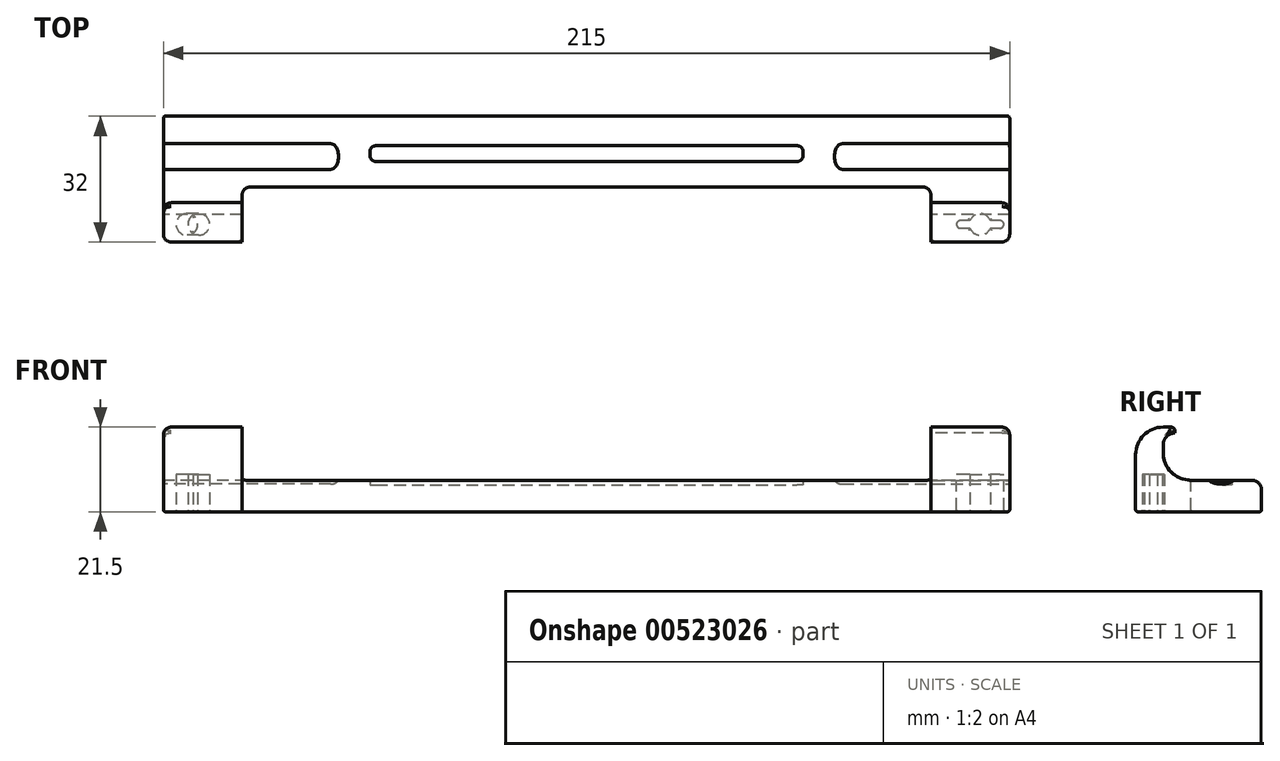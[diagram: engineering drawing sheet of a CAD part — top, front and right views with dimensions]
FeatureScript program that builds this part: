
annotation { "Feature Type Name" : "Feature", "Feature Type Description" : "" }
export const myFeature = defineFeature(function(context is Context, id is Id, definition is map)
    precondition{}
    {
        {
            var Q0;
            Q0=qCreatedBy(makeId("Right.planeOp"),FACE);
            var sketch = newSketch(context, id + "F0", { "sketchPlane" : qUnion([Q0])});
            skLineSegment(sketch, "E0", {"start": v(0, 0) * mm, "end": v(32, 0) * mm});
            skLineSegment(sketch, "E1", {"start": v(32, 0) * mm, "end": v(32, 8) * mm});
            skLineSegment(sketch, "E2", {"start": v(32, 8) * mm, "end": v(7, 8) * mm});
            skLineSegment(sketch, "E3", {"start": v(7, 8) * mm, "end": v(7, 21.5) * mm});
            skLineSegment(sketch, "E4", {"start": v(7, 21.5) * mm, "end": v(0, 21.5) * mm});
            skLineSegment(sketch, "E5", {"start": v(0, 21.5) * mm, "end": v(0, 0) * mm});
            skLineSegment(sketch, "E6", {"start": v(27.76, 8) * mm, "end": v(32, 3) * mm});
            skPoint(sketch, "E7", {"position": v(27.76, 8) * mm});
            skLineSegment(sketch, "E8.bottom", {"start": v(7, 21.5) * mm, "end": v(10, 21.5) * mm});
            skLineSegment(sketch, "E8.top", {"start": v(7, 17) * mm, "end": v(10, 17) * mm});
            skLineSegment(sketch, "E8.left", {"start": v(7, 21.5) * mm, "end": v(7, 17) * mm});
            skLineSegment(sketch, "E8.right", {"start": v(10, 21.5) * mm, "end": v(10, 17) * mm});
            skCircle(sketch, "E9", {"center": v(10, 17) * mm, "radius": 3 * mm});
            skPoint(sketch, "E10", {"position": v(10, 20) * mm});
            skSolve(sketch);
        }
        {
            var Q0;
            Q0=qCreatedBy(makeId("Right.planeOp"),FACE);
            var sketch = newSketch(context, id + "F1", { "sketchPlane" : qUnion([Q0])});
            skLineSegment(sketch, "E11.bottom", {"start": v(20.5, 8) * mm, "end": v(24.5, 8) * mm});
            skLineSegment(sketch, "E11.top", {"start": v(20.5, 6.8) * mm, "end": v(24.5, 6.8) * mm});
            skLineSegment(sketch, "E11.left", {"start": v(20.5, 8) * mm, "end": v(20.5, 6.8) * mm});
            skLineSegment(sketch, "E11.right", {"start": v(24.5, 8) * mm, "end": v(24.5, 6.8) * mm});
            skSolve(sketch);
        }
        {
            var Q0;
            {var subQ4=sQuery(id+"F0.wireOp",EDGE,"E0");Q0=makeQuery(id+"F0.imprint","IMPRINT",FACE,{"disambiguationData":[TD([[makeQuery(id+"F0.imprint","IMPRINT",EDGE,{"derivedFrom":subQ4}),1.0]])]});}
            var Q1;
            {var subQ0=sQuery(id+"F0.wireOp",EDGE,"E8.bottom");Q1=makeQuery(id+"F0.imprint","IMPRINT",FACE,{"disambiguationData":[TD([[makeQuery(id+"F0.imprint","IMPRINT",EDGE,{"derivedFrom":subQ0}),-1.0]])]});}
            var Q2;
            {var subQ3=sQuery(id+"F0.wireOp",EDGE,"E6");Q2=makeQuery(id+"F0.imprint","IMPRINT",FACE,{"disambiguationData":[TD([[makeQuery(id+"F0.imprint","IMPRINT",EDGE,{"derivedFrom":subQ3}),1.0]])]});}
            extrude(context, id + "F2", {"entities" : qUnion([Q0, Q1, Q2]), "endBound" : BoundingType.SYMMETRIC, "depth" : 215 * mm, "offsetDistance" : 25 * mm});
        }
        {
            var Q0;
            Q0 = qSketchRegion(id + "F1", true);
            extrude(context, id + "F3", {"entities" : qUnion([Q0]), "operationType" : NewBodyOperationType.REMOVE, "endBound" : BoundingType.SYMMETRIC, "oppositeDirection" : true, "depth" : 110 * mm, "offsetDistance" : 25 * mm});
        }
        {
            var Q0;
            Q0=makeQuery(id+"F2.opExtrude","SWEPT_FACE",FACE,{"disambiguationData":[OSD([sQuery(id+"F0.wireOp",EDGE,"E5")])]});
            var sketch = newSketch(context, id + "F4", { "sketchPlane" : qUnion([Q0])});
            skLineSegment(sketch, "E12", {"start": v(0, 50.18) * mm, "end": v(0, -36.06) * mm, "construction": true});
            skLineSegment(sketch, "E13.bottom", {"start": v(-87.5, 21.5) * mm, "end": v(87.5, 21.5) * mm});
            skLineSegment(sketch, "E13.top", {"start": v(-87.5, 8) * mm, "end": v(87.5, 8) * mm});
            skLineSegment(sketch, "E13.left", {"start": v(87.5, 21.5) * mm, "end": v(87.5, 8) * mm});
            skLineSegment(sketch, "E13.right", {"start": v(-87.5, 21.5) * mm, "end": v(-87.5, 8) * mm});
            skSolve(sketch);
        }
        {
            var Q0;
            Q0 = qSketchRegion(id + "F4", true);
            extrude(context, id + "F5", {"entities" : qUnion([Q0]), "operationType" : NewBodyOperationType.REMOVE, "endBound" : BoundingType.THROUGH_ALL, "oppositeDirection" : true, "depth" : 25 * mm, "offsetDistance" : 25 * mm});
        }
        {
            var Q0;
            Q0=makeQuery(id+"F5.boolean.opBoolean","MERGE",FACE,{"derivedFrom":[makeQuery(id+"F2.opExtrude","SWEPT_FACE",FACE,{"disambiguationData":[OSD([sQuery(id+"F0.wireOp",EDGE,"E2")])]}),makeQuery(id+"F5.opExtrude","SWEPT_FACE",FACE,{"disambiguationData":[OSD([sQuery(id+"F4.wireOp",EDGE,"E13.top")])]})]});
            var sketch = newSketch(context, id + "F6", { "sketchPlane" : qUnion([Q0])});
            skLineSegment(sketch, "E14.bottom", {"start": v(-87.5, 0) * mm, "end": v(87.5, 0) * mm});
            skLineSegment(sketch, "E14.top", {"start": v(-87.5, 14) * mm, "end": v(87.5, 14) * mm});
            skLineSegment(sketch, "E14.left", {"start": v(-87.5, 0) * mm, "end": v(-87.5, 14) * mm});
            skLineSegment(sketch, "E14.right", {"start": v(87.5, 0) * mm, "end": v(87.5, 14) * mm});
            skSolve(sketch);
        }
        {
            var Q0;
            Q0 = qSketchRegion(id + "F6", true);
            extrude(context, id + "F7", {"entities" : qUnion([Q0]), "operationType" : NewBodyOperationType.REMOVE, "endBound" : BoundingType.THROUGH_ALL, "oppositeDirection" : true, "depth" : 25 * mm, "offsetDistance" : 25 * mm});
        }
        {
            var Q0;
            Q0=makeQuery(id+"F2.opExtrude","CAP_FACE",FACE,{"disambiguationData":[OSD([sQuery(id+"F0.wireOp",EDGE,"E0"),sQuery(id+"F0.wireOp",EDGE,"E1"),sQuery(id+"F0.wireOp",EDGE,"E2"),sQuery(id+"F0.wireOp",EDGE,"E3"),sQuery(id+"F0.wireOp",EDGE,"E4"),sQuery(id+"F0.wireOp",EDGE,"E5"),sQuery(id+"F0.wireOp",EDGE,"E8.bottom"),sQuery(id+"F0.wireOp",EDGE,"E8.right"),sQuery(id+"F0.wireOp",EDGE,"E9")])],"isStart":true});
            var sketch = newSketch(context, id + "F8", { "sketchPlane" : qUnion([Q0])});
            skCircle(sketch, "E15", {"center": v(-21.75, 12.78) * mm, "radius": 5.78 * mm});
            skPoint(sketch, "E16", {"position": v(-25, 8) * mm});
            skPoint(sketch, "E17", {"position": v(-18.5, 8) * mm});
            skPoint(sketch, "E18", {"position": v(-21.75, 7) * mm});
            skSolve(sketch);
        }
        {
            var Q0;
            {var subQ0=sQuery(id+"F8.wireOp",EDGE,"E15");var subQ1=makeQuery(id+"F2.opExtrude","CAP_EDGE",EDGE,{"disambiguationData":[OSD([sQuery(id+"F0.wireOp",EDGE,"E2")])],"isStart":true});var subQ2=makeQuery(id+"F8.imprint","INTERSECT",VERTEX,{"disambiguationData":[OD(0.0)],"derivedFrom":[subQ1,subQ0]});Q0=makeQuery(id+"F8.imprint","IMPRINT",FACE,{"disambiguationData":[TD([[makeQuery(id+"F8.imprint","IMPRINT",EDGE,{"disambiguationData":[TD([[subQ2,-1.0]])],"derivedFrom":subQ0}),1.0]])]});}
            var Q1;
            {var subQ0=sQuery(id+"F8.wireOp",EDGE,"E15");var subQ1=makeQuery(id+"F2.opExtrude","CAP_EDGE",EDGE,{"disambiguationData":[OSD([sQuery(id+"F0.wireOp",EDGE,"E2")])],"isStart":true});var subQ2=makeQuery(id+"F8.imprint","INTERSECT",VERTEX,{"disambiguationData":[OD(0.0)],"derivedFrom":[subQ1,subQ0]});Q1=makeQuery(id+"F8.imprint","IMPRINT",FACE,{"disambiguationData":[TD([[makeQuery(id+"F8.imprint","IMPRINT",EDGE,{"disambiguationData":[TD([[subQ2,1.0]])],"derivedFrom":subQ0}),1.0]])]});}
            extrude(context, id + "F9", {"entities" : qUnion([Q0, Q1]), "oppositeDirection" : true, "depth" : 45 * mm, "offsetDistance" : 25 * mm});
        }
        {
            var Q0;
            Q0=makeQuery(id+"F9.opExtrude","SWEPT_BODY",BODY,{"disambiguationData":[OSD([sQuery(id+"F8.wireOp",EDGE,"E15")])]});
            var Q1;
            Q1=qCreatedBy(makeId("Right.planeOp"),FACE);
            mirror(context, id + "F10", {"entities" : qUnion([Q0]), "mirrorPlane" : qUnion([Q1])});
        }
        {
            var Q0;
            Q0=makeQuery(id+"F9.opExtrude","SWEPT_BODY",BODY,{"disambiguationData":[OSD([sQuery(id+"F8.wireOp",EDGE,"E15")])]});
            var Q1;
            Q1=makeQuery(id+"F10.opPattern","COPY",BODY,{"derivedFrom":makeQuery(id+"F9.opExtrude","SWEPT_BODY",BODY,{"disambiguationData":[OSD([sQuery(id+"F8.wireOp",EDGE,"E15")])]}),"instanceName":"1"});
            var Q2;
            Q2=makeQuery(id+"F2.opExtrude","SWEPT_BODY",BODY,{"disambiguationData":[OSD([sQuery(id+"F0.wireOp",EDGE,"E0"),sQuery(id+"F0.wireOp",EDGE,"E1"),sQuery(id+"F0.wireOp",EDGE,"E2"),sQuery(id+"F0.wireOp",EDGE,"E3"),sQuery(id+"F0.wireOp",EDGE,"E4"),sQuery(id+"F0.wireOp",EDGE,"E5"),sQuery(id+"F0.wireOp",EDGE,"E8.bottom"),sQuery(id+"F0.wireOp",EDGE,"E8.right"),sQuery(id+"F0.wireOp",EDGE,"E9")])]});
            booleanBodies(context, id + "F11", {"operationType" : BooleanOperationType.SUBTRACTION, "tools" : qUnion([Q0, Q1]), "targets" : qUnion([Q2])});
        }
        {
            var Q0;
            {var subQ0=sQuery(id+"F0.wireOp",EDGE,"E3");var subQ1=sQuery(id+"F0.wireOp",EDGE,"E2");Q0=makeQuery(id+"F5.boolean.opBoolean","SPLIT",EDGE,{"disambiguationData":[TD([makeQuery(id+"F5.opExtrude","SWEPT_FACE",FACE,{"disambiguationData":[OSD([sQuery(id+"F4.wireOp",EDGE,"E13.right")])]})])],"derivedFrom":makeQuery(id+"F2.opExtrude","SWEPT_EDGE",EDGE,{"disambiguationData":[OSD([subQ1,subQ0])]})});}
            var Q1;
            {var subQ0=sQuery(id+"F0.wireOp",EDGE,"E3");var subQ1=sQuery(id+"F0.wireOp",EDGE,"E2");Q1=makeQuery(id+"F5.boolean.opBoolean","SPLIT",EDGE,{"disambiguationData":[TD([makeQuery(id+"F5.opExtrude","SWEPT_FACE",FACE,{"disambiguationData":[OSD([sQuery(id+"F4.wireOp",EDGE,"E13.left")])]})])],"derivedFrom":makeQuery(id+"F2.opExtrude","SWEPT_EDGE",EDGE,{"disambiguationData":[OSD([subQ1,subQ0])]})});}
            var Q2;
            {var subQ1=sQuery(id+"F0.wireOp",EDGE,"E5");var subQ2=sQuery(id+"F0.wireOp",EDGE,"E4");Q2=makeQuery(id+"F5.boolean.opBoolean","SPLIT",EDGE,{"disambiguationData":[TD([makeQuery(id+"F5.opExtrude","SWEPT_FACE",FACE,{"disambiguationData":[OSD([sQuery(id+"F4.wireOp",EDGE,"E13.right")])]})])],"derivedFrom":makeQuery(id+"F2.opExtrude","SWEPT_EDGE",EDGE,{"disambiguationData":[OSD([subQ2,subQ1])]})});}
            var Q3;
            {var subQ1=sQuery(id+"F0.wireOp",EDGE,"E5");var subQ2=sQuery(id+"F0.wireOp",EDGE,"E4");Q3=makeQuery(id+"F5.boolean.opBoolean","SPLIT",EDGE,{"disambiguationData":[TD([makeQuery(id+"F5.opExtrude","SWEPT_FACE",FACE,{"disambiguationData":[OSD([sQuery(id+"F4.wireOp",EDGE,"E13.left")])]})])],"derivedFrom":makeQuery(id+"F2.opExtrude","SWEPT_EDGE",EDGE,{"disambiguationData":[OSD([subQ2,subQ1])]})});}
            fillet(context, id + "F12", {"entities" : qUnion([Q0, Q1, Q2, Q3]), "radius" : 7 * mm, "tangentPropagation" : true, "allowEdgeOverflow" : false});
        }
        {
            var Q0;
            Q0=makeQuery(id+"F2.opExtrude","SWEPT_EDGE",EDGE,{"disambiguationData":[OSD([sQuery(id+"F0.wireOp",EDGE,"E1"),sQuery(id+"F0.wireOp",EDGE,"E2")])]});
            var Q1;
            Q1=makeQuery(id+"F11.opBoolean","COPY",EDGE,{"derivedFrom":makeQuery(id+"F10.opPattern","COPY",EDGE,{"derivedFrom":makeQuery(id+"F9.opExtrude","CAP_EDGE",EDGE,{"disambiguationData":[OSD([sQuery(id+"F8.wireOp",EDGE,"E15")])],"isStart":false}),"instanceName":"1"})});
            var Q2;
            Q2=makeQuery(id+"F11.opBoolean","COPY",EDGE,{"derivedFrom":makeQuery(id+"F9.opExtrude","CAP_EDGE",EDGE,{"disambiguationData":[OSD([sQuery(id+"F8.wireOp",EDGE,"E15")])],"isStart":false})});
            fillet(context, id + "F13", {"entities" : qUnion([Q0, Q1, Q2]), "radius" : 2.5 * mm, "tangentPropagation" : true, "allowEdgeOverflow" : false});
        }
        {
            var Q0;
            {var subQ0=sQuery(id+"F0.wireOp",EDGE,"E8.right");var subQ1=sQuery(id+"F0.wireOp",EDGE,"E8.bottom");Q0=makeQuery(id+"F5.boolean.opBoolean","SPLIT",EDGE,{"disambiguationData":[TD([makeQuery(id+"F5.opExtrude","SWEPT_FACE",FACE,{"disambiguationData":[OSD([sQuery(id+"F4.wireOp",EDGE,"E13.right")])]})])],"derivedFrom":makeQuery(id+"F2.opExtrude","SWEPT_EDGE",EDGE,{"disambiguationData":[OSD([subQ1,subQ0])]})});}
            var Q1;
            {var subQ0=sQuery(id+"F0.wireOp",EDGE,"E8.right");var subQ1=sQuery(id+"F0.wireOp",EDGE,"E8.bottom");Q1=makeQuery(id+"F5.boolean.opBoolean","SPLIT",EDGE,{"disambiguationData":[TD([makeQuery(id+"F5.opExtrude","SWEPT_FACE",FACE,{"disambiguationData":[OSD([sQuery(id+"F4.wireOp",EDGE,"E13.left")])]})])],"derivedFrom":makeQuery(id+"F2.opExtrude","SWEPT_EDGE",EDGE,{"disambiguationData":[OSD([subQ1,subQ0])]})});}
            fillet(context, id + "F14", {"entities" : qUnion([Q0, Q1]), "radius" : 1 * mm, "tangentPropagation" : true, "allowEdgeOverflow" : false});
        }
        {
            var Q0;
            Q0=makeQuery(id+"F5.boolean.opBoolean","COPY",EDGE,{"derivedFrom":makeQuery(id+"F5.opExtrude","SWEPT_EDGE",EDGE,{"disambiguationData":[OSD([sQuery(id+"F4.wireOp",EDGE,"E13.top"),sQuery(id+"F4.wireOp",EDGE,"E13.left")])]})});
            var Q1;
            Q1=makeQuery(id+"F5.boolean.opBoolean","COPY",EDGE,{"derivedFrom":makeQuery(id+"F5.opExtrude","CAP_EDGE",EDGE,{"disambiguationData":[OSD([sQuery(id+"F4.wireOp",EDGE,"E13.right")])],"isStart":true})});
            var Q2;
            Q2=makeQuery(id+"F5.boolean.opBoolean","COPY",EDGE,{"derivedFrom":makeQuery(id+"F5.opExtrude","CAP_EDGE",EDGE,{"disambiguationData":[OSD([sQuery(id+"F4.wireOp",EDGE,"E13.left")])],"isStart":true})});
            var Q3;
            Q3=makeQuery(id+"F5.boolean.opBoolean","COPY",EDGE,{"derivedFrom":makeQuery(id+"F5.opExtrude","SWEPT_EDGE",EDGE,{"disambiguationData":[OSD([sQuery(id+"F4.wireOp",EDGE,"E13.top"),sQuery(id+"F4.wireOp",EDGE,"E13.right")])]})});
            var Q4;
            Q4=makeQuery(id+"F2.opExtrude","CAP_EDGE",EDGE,{"disambiguationData":[OSD([sQuery(id+"F0.wireOp",EDGE,"E5")])],"isStart":true});
            var Q5;
            Q5=makeQuery(id+"F2.opExtrude","CAP_EDGE",EDGE,{"disambiguationData":[OSD([sQuery(id+"F0.wireOp",EDGE,"E5")])],"isStart":false});
            var Q6;
            Q6=makeQuery(id+"F7.boolean.opBoolean","COPY",EDGE,{"derivedFrom":makeQuery(id+"F7.opExtrude","SWEPT_EDGE",EDGE,{"disambiguationData":[OSD([sQuery(id+"F6.wireOp",EDGE,"E14.top"),sQuery(id+"F6.wireOp",EDGE,"E14.left")])]})});
            var Q7;
            Q7=makeQuery(id+"F7.boolean.opBoolean","COPY",EDGE,{"derivedFrom":makeQuery(id+"F7.opExtrude","SWEPT_EDGE",EDGE,{"disambiguationData":[OSD([sQuery(id+"F6.wireOp",EDGE,"E14.top"),sQuery(id+"F6.wireOp",EDGE,"E14.right")])]})});
            fillet(context, id + "F15", {"entities" : qUnion([Q0, Q1, Q2, Q3, Q4, Q5, Q6, Q7]), "radius" : 2 * mm, "tangentPropagation" : true, "allowEdgeOverflow" : false});
        }
        {
            var Q0;
            Q0=makeQuery(id+"F2.opExtrude","CAP_EDGE",EDGE,{"disambiguationData":[OSD([sQuery(id+"F0.wireOp",EDGE,"E6")])],"isStart":false});
            var Q1;
            Q1=makeQuery(id+"F2.opExtrude","CAP_EDGE",EDGE,{"disambiguationData":[OSD([sQuery(id+"F0.wireOp",EDGE,"E2")])],"isStart":true});
            var Q2;
            Q2=makeQuery(id+"F2.opExtrude","CAP_EDGE",EDGE,{"disambiguationData":[OSD([sQuery(id+"F0.wireOp",EDGE,"E1")])],"isStart":false});
            var Q3;
            Q3=makeQuery(id+"F11.opBoolean","COPY",EDGE,{"derivedFrom":makeQuery(id+"F10.opPattern","COPY",EDGE,{"derivedFrom":makeQuery(id+"F9.opExtrude","CAP_EDGE",EDGE,{"disambiguationData":[OSD([sQuery(id+"F8.wireOp",EDGE,"E15")])],"isStart":true}),"instanceName":"1"})});
            var Q4;
            Q4=makeQuery(id+"F11.opBoolean","COPY",EDGE,{"derivedFrom":makeQuery(id+"F9.opExtrude","CAP_EDGE",EDGE,{"disambiguationData":[OSD([sQuery(id+"F8.wireOp",EDGE,"E15")])],"isStart":true})});
            fillet(context, id + "F16", {"entities" : qUnion([Q0, Q1, Q2, Q3, Q4]), "radius" : 0.5 * mm, "tangentPropagation" : true, "allowEdgeOverflow" : false});
        }
        {
            var Q0;
            Q0=makeQuery(id+"F3.boolean.opBoolean","COPY",EDGE,{"derivedFrom":makeQuery(id+"F3.opExtrude","CAP_EDGE",EDGE,{"disambiguationData":[OSD([sQuery(id+"F1.wireOp",EDGE,"E11.right")])],"isStart":false})});
            var Q1;
            Q1=makeQuery(id+"F3.boolean.opBoolean","COPY",EDGE,{"derivedFrom":makeQuery(id+"F3.opExtrude","CAP_EDGE",EDGE,{"disambiguationData":[OSD([sQuery(id+"F1.wireOp",EDGE,"E11.left")])],"isStart":false})});
            var Q2;
            Q2=makeQuery(id+"F3.boolean.opBoolean","COPY",EDGE,{"derivedFrom":makeQuery(id+"F3.opExtrude","CAP_EDGE",EDGE,{"disambiguationData":[OSD([sQuery(id+"F1.wireOp",EDGE,"E11.right")])],"isStart":true})});
            var Q3;
            Q3=makeQuery(id+"F3.boolean.opBoolean","COPY",EDGE,{"derivedFrom":makeQuery(id+"F3.opExtrude","CAP_EDGE",EDGE,{"disambiguationData":[OSD([sQuery(id+"F1.wireOp",EDGE,"E11.left")])],"isStart":true})});
            fillet(context, id + "F17", {"entities" : qUnion([Q0, Q1, Q2, Q3]), "radius" : 1.5 * mm, "tangentPropagation" : true, "allowEdgeOverflow" : false});
        }
        {
            var Q0;
            Q0=makeQuery(id+"F2.opExtrude","SWEPT_FACE",FACE,{"disambiguationData":[OSD([sQuery(id+"F0.wireOp",EDGE,"E0")])]});
            var sketch = newSketch(context, id + "F18", { "sketchPlane" : qUnion([Q0])});
            skCircle(sketch, "E19", {"center": v(100.01, -4.5) * mm, "radius": 2.75 * mm});
            skCircle(sketch, "E20", {"center": v(-98.51, -4.5) * mm, "radius": 2.75 * mm});
            skCircle(sketch, "E21", {"center": v(-101.51, -4.5) * mm, "radius": 2.75 * mm});
            skLineSegment(sketch, "E22.bottom", {"start": v(-98.51, -7.25) * mm, "end": v(-101.51, -7.25) * mm});
            skLineSegment(sketch, "E22.top", {"start": v(-98.51, -1.75) * mm, "end": v(-101.51, -1.75) * mm});
            skLineSegment(sketch, "E22.left", {"start": v(-98.51, -7.25) * mm, "end": v(-98.51, -1.75) * mm});
            skLineSegment(sketch, "E22.right", {"start": v(-101.51, -7.25) * mm, "end": v(-101.51, -1.75) * mm});
            skLineSegment(sketch, "E23", {"start": v(-100.01, -7.25) * mm, "end": v(-100.01, -1.75) * mm});
            skLineSegment(sketch, "E24.bottom", {"start": v(106.01, -5.5) * mm, "end": v(94.01, -5.5) * mm});
            skLineSegment(sketch, "E24.top", {"start": v(106.01, -3.5) * mm, "end": v(94.01, -3.5) * mm});
            skLineSegment(sketch, "E24.left", {"start": v(106.01, -5.5) * mm, "end": v(106.01, -3.5) * mm});
            skLineSegment(sketch, "E24.right", {"start": v(94.01, -5.5) * mm, "end": v(94.01, -3.5) * mm});
            skLineSegment(sketch, "E25", {"start": v(100.01, -4.5) * mm, "end": v(100.01, -17.35) * mm, "construction": true});
            skLineSegment(sketch, "E26", {"start": v(100.01, -4.5) * mm, "end": v(69.96, -4.5) * mm, "construction": true});
            skLineSegment(sketch, "E27", {"start": v(0, -35.09) * mm, "end": v(0, 41.16) * mm, "construction": true});
            skPoint(sketch, "E28", {"position": v(-100.01, -4.5) * mm});
            skSolve(sketch);
        }
        {
            var Q0;
            Q0 = qSketchRegion(id + "F18", true);
            var Q1;
            {var subQ0=sQuery(id+"F18.wireOp",EDGE,"E23");var subQ1=sQuery(id+"F18.wireOp",EDGE,"E21");var subQ2=sQuery(id+"F18.wireOp",EDGE,"E20");var subQ3=makeQuery(id+"F18.imprint","INTERSECT",VERTEX,{"disambiguationData":[OD(0.0)],"derivedFrom":[subQ2,subQ1,subQ0]});Q1=makeQuery(id+"F18.imprint","IMPRINT",FACE,{"disambiguationData":[TD([[makeQuery(id+"F18.imprint","IMPRINT",EDGE,{"disambiguationData":[TD([[subQ3,-1.0]])],"derivedFrom":subQ2}),1.0]])]});}
            var Q2;
            {var subQ0=sQuery(id+"F18.wireOp",EDGE,"E23");var subQ1=sQuery(id+"F18.wireOp",EDGE,"E21");var subQ2=sQuery(id+"F18.wireOp",EDGE,"E20");var subQ3=makeQuery(id+"F18.imprint","INTERSECT",VERTEX,{"disambiguationData":[OD(0.0)],"derivedFrom":[subQ2,subQ1,subQ0]});Q2=makeQuery(id+"F18.imprint","IMPRINT",FACE,{"disambiguationData":[TD([[makeQuery(id+"F18.imprint","IMPRINT",EDGE,{"disambiguationData":[TD([[subQ3,1.0]])],"derivedFrom":subQ1}),1.0]])]});}
            extrude(context, id + "F19", {"entities" : qUnion([Q0, Q1, Q2]), "operationType" : NewBodyOperationType.REMOVE, "oppositeDirection" : true, "depth" : 9.5 * mm, "offsetDistance" : 25 * mm});
        }
        {
            var Q0;
            Q0=makeQuery(id+"F19.boolean.opBoolean","COPY",EDGE,{"derivedFrom":makeQuery(id+"F19.opExtrude","SWEPT_EDGE",EDGE,{"disambiguationData":[OSD([sQuery(id+"F18.wireOp",EDGE,"E24.top"),sQuery(id+"F18.wireOp",EDGE,"E24.left")])]})});
            var Q1;
            Q1=makeQuery(id+"F19.boolean.opBoolean","COPY",EDGE,{"derivedFrom":makeQuery(id+"F19.opExtrude","SWEPT_EDGE",EDGE,{"disambiguationData":[OSD([sQuery(id+"F18.wireOp",EDGE,"E24.bottom"),sQuery(id+"F18.wireOp",EDGE,"E24.left")])]})});
            var Q2;
            Q2=makeQuery(id+"F19.boolean.opBoolean","COPY",EDGE,{"derivedFrom":makeQuery(id+"F19.opExtrude","SWEPT_EDGE",EDGE,{"disambiguationData":[OSD([sQuery(id+"F18.wireOp",EDGE,"E24.bottom"),sQuery(id+"F18.wireOp",EDGE,"E24.right")])]})});
            var Q3;
            Q3=makeQuery(id+"F19.boolean.opBoolean","COPY",EDGE,{"derivedFrom":makeQuery(id+"F19.opExtrude","SWEPT_EDGE",EDGE,{"disambiguationData":[OSD([sQuery(id+"F18.wireOp",EDGE,"E24.top"),sQuery(id+"F18.wireOp",EDGE,"E24.right")])]})});
            fillet(context, id + "F20", {"entities" : qUnion([Q0, Q1, Q2, Q3]), "radius" : 1 * mm, "tangentPropagation" : true, "allowEdgeOverflow" : false});
        }
        {
            var Q0;
            Q0=makeQuery(id+"F2.opExtrude","SWEPT_FACE",FACE,{"disambiguationData":[OSD([sQuery(id+"F0.wireOp",EDGE,"E0")])]});
            fillet(context, id + "F21", {"entities" : qUnion([Q0]), "radius" : .5 * mm, "tangentPropagation" : true, "allowEdgeOverflow" : false});
        }
    });
